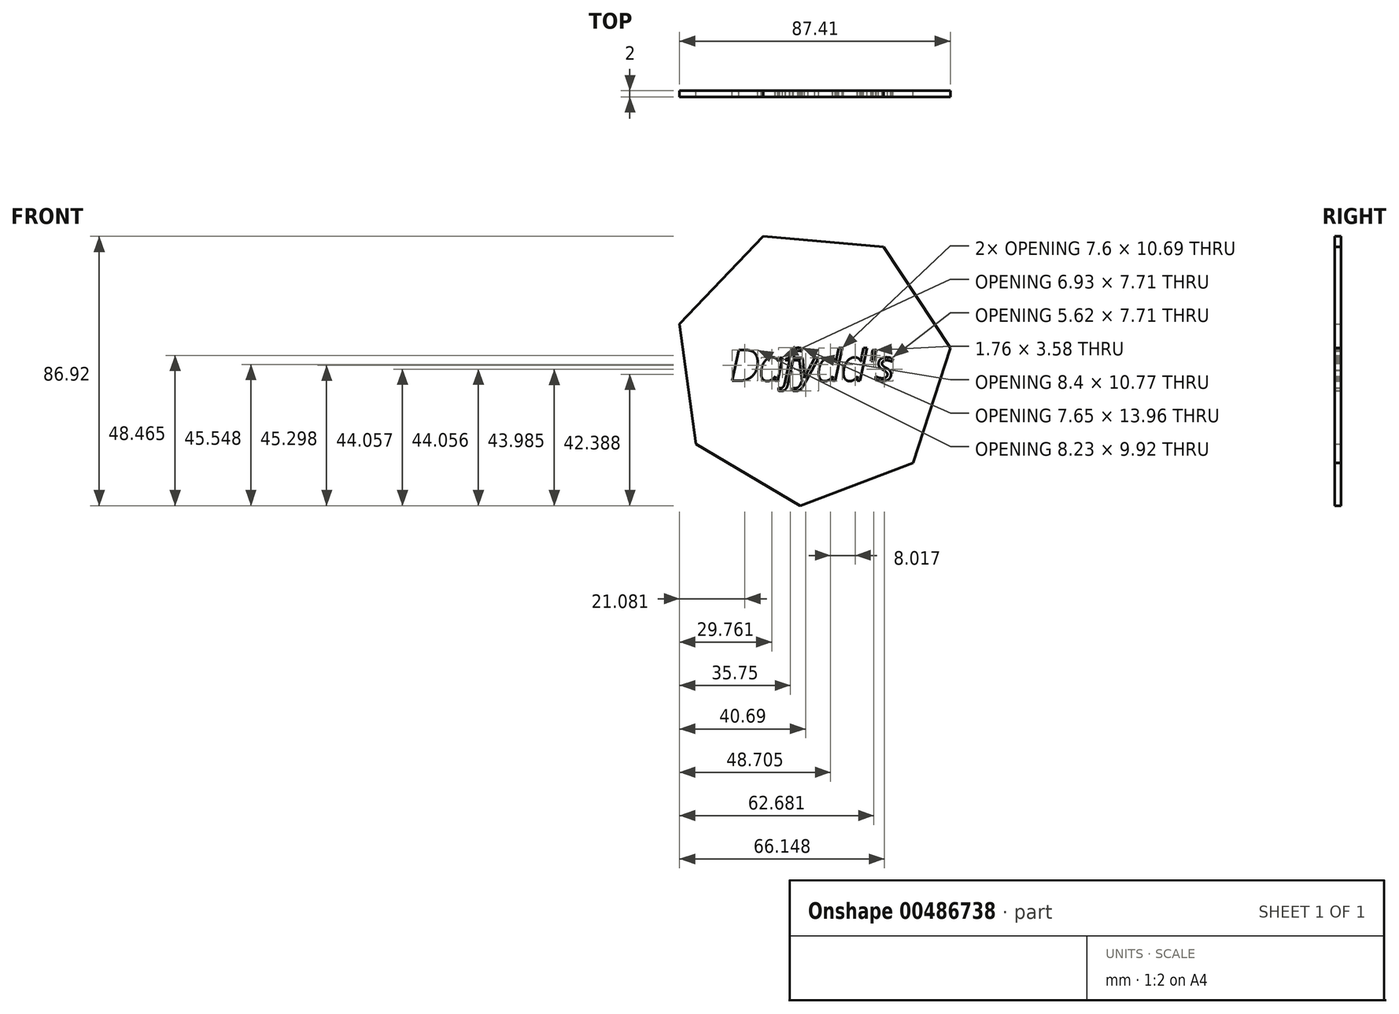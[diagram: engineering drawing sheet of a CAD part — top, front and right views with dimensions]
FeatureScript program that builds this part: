
annotation { "Feature Type Name" : "Feature", "Feature Type Description" : "" }
export const myFeature = defineFeature(function(context is Context, id is Id, definition is map)
    precondition{}
    {
        {
            var Q0;
            Q0=qCreatedBy(makeId("Front.planeOp"),FACE);
            var sketch = newSketch(context, id + "F0", { "sketchPlane" : qUnion([Q0])});
            skCircle(sketch, "E0.cCircle", {"center": v(-30.25, 32.63) * mm, "radius": 45 * mm, "construction": true});
            skLineSegment(sketch, "E0.0", {"start": v(2.33, 1.6) * mm, "end": v(-34.2, -12.2) * mm});
            skLineSegment(sketch, "E0.1", {"start": v(-34.2, -12.2) * mm, "end": v(-67.76, 7.77) * mm});
            skLineSegment(sketch, "E0.2", {"start": v(-67.76, 7.77) * mm, "end": v(-73.08, 46.45) * mm});
            skLineSegment(sketch, "E0.3", {"start": v(-73.08, 46.45) * mm, "end": v(-46.15, 74.73) * mm});
            skLineSegment(sketch, "E0.4", {"start": v(-46.15, 74.73) * mm, "end": v(-7.25, 71.3) * mm});
            skLineSegment(sketch, "E0.5", {"start": v(-7.25, 71.3) * mm, "end": v(14.33, 38.76) * mm});
            skLineSegment(sketch, "E0.6", {"start": v(14.33, 38.76) * mm, "end": v(2.33, 1.6) * mm});
            skText(sketch, "E1", { "text": "Dafydd\'s\n", "fontName": "OpenSans-Italic.ttf"});
            const initialGuessF0  = {"E1": [-0.0567, 0.02815, 1, 0, 0.01]};
            skSetInitialGuess(sketch, initialGuessF0);
            skSolve(sketch);
        }
        {
            var Q0;
            Q0 = qSketchRegion(id + "F0", true);
            extrude(context, id + "F1", {"entities" : qUnion([Q0]), "depth" : 2 * mm});
        }
    });
